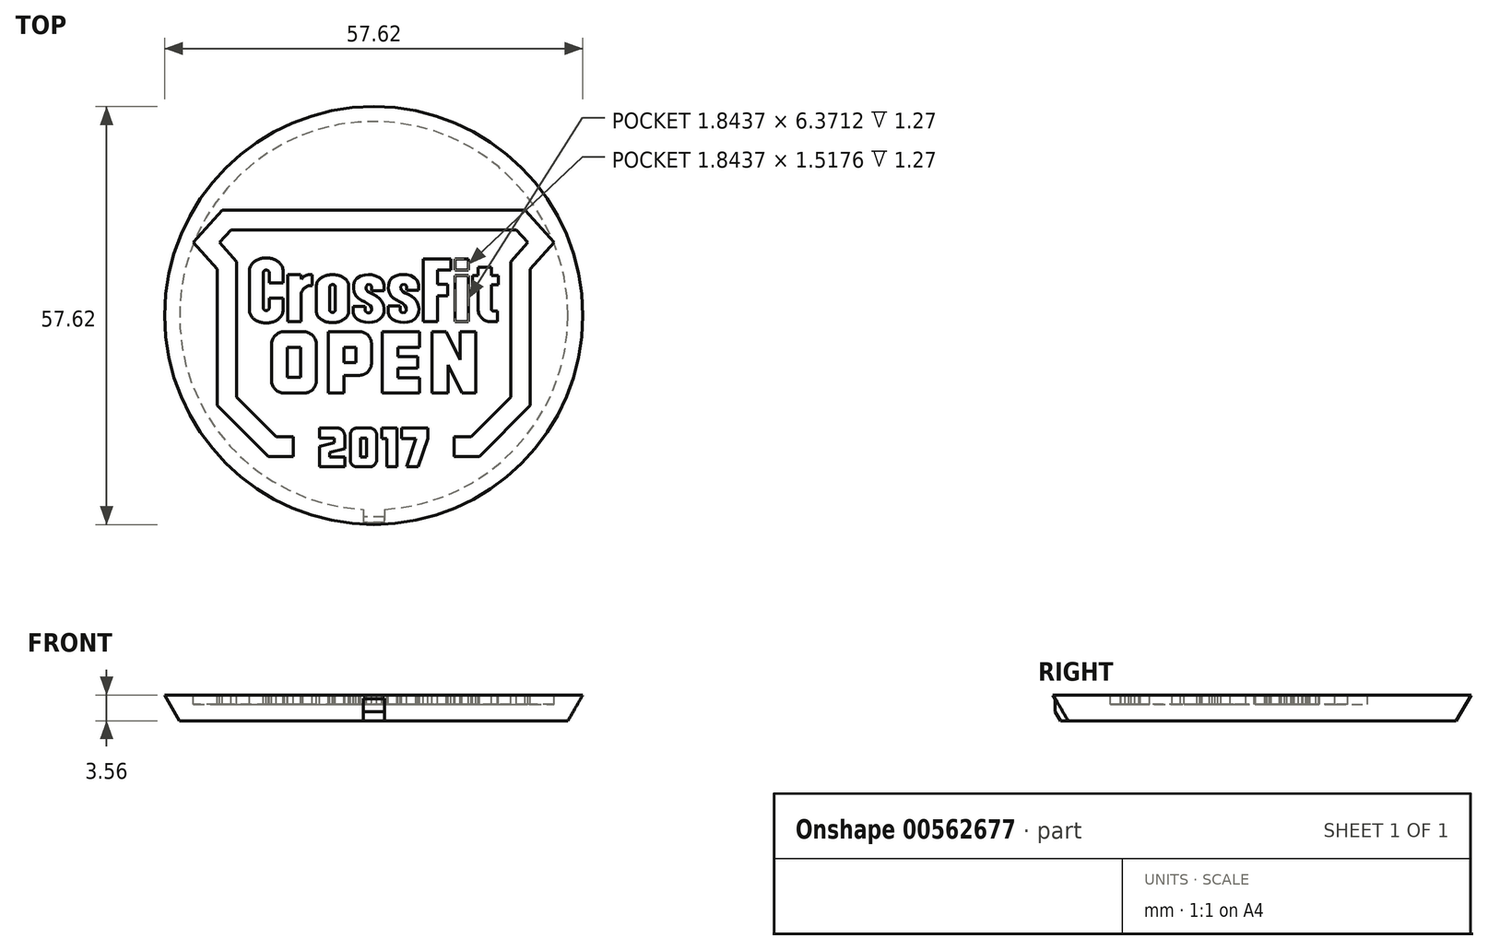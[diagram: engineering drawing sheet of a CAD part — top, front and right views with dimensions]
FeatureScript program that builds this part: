
annotation { "Feature Type Name" : "Feature", "Feature Type Description" : "" }
export const myFeature = defineFeature(function(context is Context, id is Id, definition is map)
    precondition{}
    {
        {
            var Q0;
            Q0=qCreatedBy(makeId("Top.planeOp"),FACE);
            var sketch = newSketch(context, id + "F0", { "sketchPlane" : qUnion([Q0])});
            skCircle(sketch, "E0", {"center": v(0, 0) * mm, "radius": 28.96 * mm});
            skSolve(sketch);
        }
        {
            var Q0;
            Q0=makeQuery(id+"F0.imprint","IMPRINT",FACE,{"disambiguationData":[TD([[makeQuery(id+"F0.imprint","IMPRINT",EDGE,{"derivedFrom":sQuery(id+"F0.wireOp",EDGE,"E0")}),1.0]])]});
            extrude(context, id + "F1", {"entities" : qUnion([Q0]), "depth" : 3.56 * mm, "offsetDistance" : 25.4 * mm});
        }
        {
            var Q0;
            Q0=makeQuery(id+"F1.opExtrude","CAP_FACE",FACE,{"disambiguationData":[OSD([sQuery(id+"F0.wireOp",EDGE,"E0")])],"isStart":false});
            var sketch = newSketch(context, id + "F2", { "sketchPlane" : qUnion([Q0])});
            skPoint(sketch, "E1", {"position": v(0.13, -0.67) * mm});
            skLineSegment(sketch, "E2", {"start": v(-15.2, 14.53) * mm, "end": v(-15.2, 11.82) * mm});
            skLineSegment(sketch, "E3", {"start": v(-15.2, 11.82) * mm, "end": v(-19.67, 11.82) * mm});
            skLineSegment(sketch, "E4", {"start": v(-19.67, 11.82) * mm, "end": v(-21.25, 10.06) * mm});
            skLineSegment(sketch, "E5", {"start": v(-21.25, 10.06) * mm, "end": v(-18.9, 7.43) * mm});
            skLineSegment(sketch, "E6", {"start": v(-18.9, 7.43) * mm, "end": v(-18.9, -11.25) * mm});
            skLineSegment(sketch, "E7", {"start": v(-18.9, -11.25) * mm, "end": v(-13.44, -16.74) * mm});
            skLineSegment(sketch, "E8", {"start": v(-13.44, -16.74) * mm, "end": v(-11.07, -16.74) * mm});
            skLineSegment(sketch, "E9", {"start": v(-11.07, -16.74) * mm, "end": v(-11.07, -19.45) * mm});
            skLineSegment(sketch, "E10", {"start": v(-11.07, -19.45) * mm, "end": v(-14.54, -19.45) * mm});
            skLineSegment(sketch, "E11", {"start": v(-14.54, -19.45) * mm, "end": v(-21.55, -12.4) * mm});
            skLineSegment(sketch, "E12", {"start": v(-21.55, -12.4) * mm, "end": v(-21.55, 6.37) * mm});
            skLineSegment(sketch, "E13", {"start": v(-21.55, 6.37) * mm, "end": v(-24.85, 10.06) * mm});
            skLineSegment(sketch, "E14", {"start": v(-24.85, 10.06) * mm, "end": v(-20.84, 14.53) * mm});
            skLineSegment(sketch, "E15", {"start": v(-20.84, 14.53) * mm, "end": v(-15.2, 14.53) * mm});
            skLineSegment(sketch, "E16", {"start": v(-14.42, 6) * mm, "end": v(-14.42, 4.47) * mm});
            skLineSegment(sketch, "E17", {"start": v(-14.42, 4.47) * mm, "end": v(-12.48, 4.47) * mm});
            skLineSegment(sketch, "E18", {"start": v(-12.48, 4.47) * mm, "end": v(-12.48, 6.3) * mm});
            skLineSegment(sketch, "E19", {"start": v(-17.15, 6.3) * mm, "end": v(-17.15, 0.62) * mm});
            skLineSegment(sketch, "E20", {"start": v(-14.42, 1) * mm, "end": v(-14.42, 2.43) * mm});
            skLineSegment(sketch, "E21", {"start": v(-14.42, 2.43) * mm, "end": v(-12.48, 2.43) * mm});
            skLineSegment(sketch, "E22", {"start": v(-12.48, 2.43) * mm, "end": v(-12.48, 0.62) * mm});
            skLineSegment(sketch, "E23", {"start": v(-15.2, 6) * mm, "end": v(-15.2, 1) * mm});
            skArc(sketch, "E24", {"start": v(-14.42, 6) * mm, "mid": v(-14.81, 6.27) * mm, "end": v(-15.2, 6) * mm});
            skArc(sketch, "E25", {"start": v(-15.2, 1) * mm, "mid": v(-14.81, 0.68) * mm, "end": v(-14.42, 1) * mm});
            skLineSegment(sketch, "E26", {"start": v(-9.97, 5) * mm, "end": v(-10.1, 5.63) * mm});
            skLineSegment(sketch, "E27", {"start": v(-10.1, 5.63) * mm, "end": v(-11.83, 5.63) * mm});
            skLineSegment(sketch, "E28", {"start": v(-11.83, 5.63) * mm, "end": v(-11.83, -0.85) * mm});
            skLineSegment(sketch, "E29", {"start": v(-11.83, -0.85) * mm, "end": v(-9.98, -0.85) * mm});
            skLineSegment(sketch, "E30", {"start": v(-9.98, -0.85) * mm, "end": v(-9.98, 3.1) * mm});
            skLineSegment(sketch, "E31", {"start": v(-8.5, 5.65) * mm, "end": v(-8.5, 4.11) * mm});
            skArc(sketch, "E32", {"start": v(-8.5, 5.65) * mm, "mid": v(-9.32, 5.53) * mm, "end": v(-9.97, 5) * mm});
            skArc(sketch, "E33", {"start": v(-8.5, 4.11) * mm, "mid": v(-9.44, 3.9) * mm, "end": v(-9.98, 3.1) * mm});
            skLineSegment(sketch, "E34", {"start": v(-7.89, 4.2) * mm, "end": v(-7.89, 0.46) * mm});
            skLineSegment(sketch, "E35", {"start": v(-3.47, 4.2) * mm, "end": v(-3.47, 0.46) * mm});
            skLineSegment(sketch, "E36", {"start": v(-6.05, 4.04) * mm, "end": v(-6.05, 0.68) * mm});
            skLineSegment(sketch, "E37", {"start": v(-5.3, 0.68) * mm, "end": v(-5.3, 4.04) * mm});
            skArc(sketch, "E38", {"start": v(-5.3, 4.04) * mm, "mid": v(-5.68, 4.28) * mm, "end": v(-6.05, 4.04) * mm});
            skArc(sketch, "E39", {"start": v(-6.05, 0.68) * mm, "mid": v(-5.68, 0.43) * mm, "end": v(-5.3, 0.68) * mm});
            skLineSegment(sketch, "E40", {"start": v(-5.68, 3.86) * mm, "end": v(-5.68, 0.84) * mm, "construction": true});
            skLineSegment(sketch, "E41", {"start": v(-7.89, 2.33) * mm, "end": v(-3.47, 2.33) * mm, "construction": true});
            skFitSpline(sketch, "E42.MirrorCS", {"points": [v(-3.47, 4.2) * mm, v(-3.93, 5.06) * mm, v(-4.62, 5.46) * mm, v(-5.68, 5.64) * mm], "startDerivative": vector(-0.46, 3.85) * mm, "endDerivative": vector(-4.22, 0.16) * mm});
            skFitSpline(sketch, "E43.MirrorCS", {"points": [v(-7.89, 0.46) * mm, v(-7.42, -0.4) * mm, v(-6.74, -0.8) * mm, v(-5.68, -0.98) * mm], "startDerivative": vector(0.46, -3.85) * mm, "endDerivative": vector(4.22, -0.16) * mm});
            skFitSpline(sketch, "E44.MirrorCS", {"points": [v(-3.47, 0.46) * mm, v(-3.93, -0.4) * mm, v(-4.62, -0.8) * mm, v(-5.68, -0.98) * mm], "startDerivative": vector(-0.46, -3.85) * mm, "endDerivative": vector(-4.22, -0.16) * mm});
            skFitSpline(sketch, "E45", {"points": [v(-17.15, 6.3) * mm, v(-16.64, 7.26) * mm, v(-16, 7.69) * mm, v(-14.81, 7.96) * mm], "startDerivative": vector(0.97, 4.15) * mm, "endDerivative": vector(4.22, 0.16) * mm});
            skLineSegment(sketch, "E46", {"start": v(-14.81, 5.84) * mm, "end": v(-14.81, 1.08) * mm, "construction": true});
            skFitSpline(sketch, "E47.MirrorCS", {"points": [v(-12.48, 6.3) * mm, v(-12.99, 7.26) * mm, v(-13.62, 7.69) * mm, v(-14.81, 7.96) * mm], "startDerivative": vector(-0.97, 4.15) * mm, "endDerivative": vector(-4.22, 0.16) * mm});
            skLineSegment(sketch, "E48", {"start": v(-17.15, 3.46) * mm, "end": v(-14.81, 3.46) * mm, "construction": true});
            skFitSpline(sketch, "E49.MirrorCS", {"points": [v(-17.15, 0.62) * mm, v(-16.64, -0.34) * mm, v(-16, -0.77) * mm, v(-14.81, -1.04) * mm], "startDerivative": vector(0.97, -4.15) * mm, "endDerivative": vector(4.22, -0.16) * mm});
            skFitSpline(sketch, "E50.MirrorCS", {"points": [v(-12.48, 0.62) * mm, v(-12.99, -0.34) * mm, v(-13.62, -0.77) * mm, v(-14.81, -1.04) * mm], "startDerivative": vector(-0.97, -4.15) * mm, "endDerivative": vector(-4.22, -0.16) * mm});
            skFitSpline(sketch, "E51.MirrorCS", {"points": [v(-7.89, 4.2) * mm, v(-7.42, 5.06) * mm, v(-6.74, 5.46) * mm, v(-5.68, 5.64) * mm], "startDerivative": vector(0.46, 3.85) * mm, "endDerivative": vector(4.22, 0.16) * mm});
            skLineSegment(sketch, "E52", {"start": v(-0.27, 4.07) * mm, "end": v(-0.27, 3.44) * mm});
            skLineSegment(sketch, "E53", {"start": v(-0.27, 3.44) * mm, "end": v(1.39, 3.44) * mm});
            skLineSegment(sketch, "E54", {"start": v(1.39, 3.44) * mm, "end": v(1.39, 4.25) * mm});
            skFitSpline(sketch, "E55", {"points": [v(1.39, 4.25) * mm, v(1.25, 4.73) * mm, v(0.96, 5.08) * mm, v(0.56, 5.36) * mm, v(0, 5.56) * mm, v(-0.4, 5.63) * mm, v(-0.7, 5.64) * mm, v(-1.07, 5.62) * mm, v(-1.62, 5.53) * mm, v(-2.03, 5.35) * mm, v(-2.4, 5.07) * mm, v(-2.62, 4.73) * mm, v(-2.76, 4.31) * mm, v(-2.8, 3.96) * mm, v(-2.78, 3.56) * mm, v(-2.7, 3.15) * mm, v(-2.47, 2.72) * mm, v(-2.25, 2.47) * mm, v(-1.97, 2.27) * mm, v(-1.61, 2.07) * mm, v(-1.3, 1.9) * mm, v(-1.02, 1.76) * mm, v(-0.75, 1.6) * mm, v(-0.5, 1.4) * mm, v(-0.41, 1.28) * mm, v(-0.32, 1.08) * mm, v(-0.3, 0.79) * mm, v(-0.34, 0.57) * mm, v(-0.46, 0.43) * mm, v(-0.64, 0.38) * mm, v(-0.84, 0.39) * mm, v(-1.03, 0.44) * mm, v(-1.16, 0.63) * mm], "startDerivative": vector(-2.14, 14.98) * mm, "endDerivative": vector(-3.94, 13.1) * mm});
            skLineSegment(sketch, "E56", {"start": v(-2.83, 0.39) * mm, "end": v(-2.83, 1.28) * mm});
            skLineSegment(sketch, "E57", {"start": v(-2.83, 1.28) * mm, "end": v(-1.16, 1.28) * mm});
            skLineSegment(sketch, "E58", {"start": v(-1.16, 1.28) * mm, "end": v(-1.16, 0.63) * mm});
            skFitSpline(sketch, "E59", {"points": [v(-2.83, 0.39) * mm, v(-2.67, -0.07) * mm, v(-2.35, -0.45) * mm, v(-1.98, -0.69) * mm, v(-1.5, -0.86) * mm, v(-1.03, -0.94) * mm, v(-0.7, -0.95) * mm, v(-0.34, -0.94) * mm, v(0.21, -0.84) * mm, v(0.6, -0.67) * mm, v(0.97, -0.39) * mm, v(1.22, -0.06) * mm, v(1.37, 0.3) * mm, v(1.42, 0.75) * mm, v(1.4, 1.11) * mm, v(1.3, 1.54) * mm, v(1.1, 1.95) * mm, v(0.87, 2.26) * mm, v(0.6, 2.5) * mm, v(0.3, 2.7) * mm, v(0, 2.88) * mm, v(-0.33, 3.05) * mm, v(-0.58, 3.18) * mm, v(-0.81, 3.31) * mm, v(-0.96, 3.44) * mm, v(-1.07, 3.64) * mm, v(-1.08, 3.86) * mm, v(-1.06, 4.07) * mm, v(-0.94, 4.24) * mm, v(-0.75, 4.3) * mm, v(-0.56, 4.29) * mm, v(-0.4, 4.23) * mm, v(-0.27, 4.07) * mm], "startDerivative": vector(2.14, -14.98) * mm, "endDerivative": vector(3.94, -13.1) * mm});
            skLineSegment(sketch, "E60", {"start": v(4.54, 4.08) * mm, "end": v(4.54, 3.45) * mm});
            skLineSegment(sketch, "E61", {"start": v(4.54, 3.45) * mm, "end": v(6.2, 3.45) * mm});
            skLineSegment(sketch, "E62", {"start": v(6.2, 3.45) * mm, "end": v(6.2, 4.26) * mm});
            skFitSpline(sketch, "E63", {"points": [v(6.2, 4.26) * mm, v(6.06, 4.74) * mm, v(5.77, 5.1) * mm, v(5.37, 5.37) * mm, v(4.81, 5.57) * mm, v(4.4, 5.64) * mm, v(4.11, 5.65) * mm, v(3.74, 5.63) * mm, v(3.2, 5.54) * mm, v(2.78, 5.36) * mm, v(2.42, 5.08) * mm, v(2.2, 4.74) * mm, v(2.05, 4.32) * mm, v(2.02, 3.97) * mm, v(2.03, 3.57) * mm, v(2.11, 3.16) * mm, v(2.34, 2.73) * mm, v(2.56, 2.48) * mm, v(2.84, 2.28) * mm, v(3.2, 2.08) * mm, v(3.52, 1.92) * mm, v(3.8, 1.77) * mm, v(4.06, 1.6) * mm, v(4.3, 1.41) * mm, v(4.4, 1.3) * mm, v(4.5, 1.09) * mm, v(4.5, 0.8) * mm, v(4.47, 0.58) * mm, v(4.35, 0.44) * mm, v(4.17, 0.39) * mm, v(3.97, 0.4) * mm, v(3.78, 0.45) * mm, v(3.65, 0.64) * mm], "startDerivative": vector(-2.14, 14.98) * mm, "endDerivative": vector(-3.94, 13.1) * mm});
            skLineSegment(sketch, "E64", {"start": v(1.98, 0.4) * mm, "end": v(1.98, 1.3) * mm});
            skLineSegment(sketch, "E65", {"start": v(1.98, 1.3) * mm, "end": v(3.65, 1.3) * mm});
            skLineSegment(sketch, "E66", {"start": v(3.65, 1.3) * mm, "end": v(3.65, 0.64) * mm});
            skFitSpline(sketch, "E67", {"points": [v(1.98, 0.4) * mm, v(2.14, -0.06) * mm, v(2.46, -0.44) * mm, v(2.83, -0.68) * mm, v(3.31, -0.85) * mm, v(3.78, -0.93) * mm, v(4.12, -0.95) * mm, v(4.47, -0.93) * mm, v(5.02, -0.83) * mm, v(5.42, -0.66) * mm, v(5.78, -0.38) * mm, v(6.03, -0.05) * mm, v(6.18, 0.32) * mm, v(6.23, 0.76) * mm, v(6.2, 1.12) * mm, v(6.12, 1.55) * mm, v(5.92, 1.96) * mm, v(5.68, 2.27) * mm, v(5.4, 2.5) * mm, v(5.1, 2.71) * mm, v(4.8, 2.89) * mm, v(4.48, 3.06) * mm, v(4.23, 3.2) * mm, v(4, 3.32) * mm, v(3.85, 3.45) * mm, v(3.74, 3.65) * mm, v(3.73, 3.87) * mm, v(3.75, 4.08) * mm, v(3.87, 4.25) * mm, v(4.06, 4.3) * mm, v(4.25, 4.3) * mm, v(4.42, 4.24) * mm, v(4.54, 4.08) * mm], "startDerivative": vector(2.14, -14.98) * mm, "endDerivative": vector(3.94, -13.1) * mm});
            skLineSegment(sketch, "E68", {"start": v(10.61, 7.8) * mm, "end": v(6.85, 7.8) * mm});
            skLineSegment(sketch, "E69", {"start": v(6.85, 7.8) * mm, "end": v(6.85, -0.85) * mm});
            skLineSegment(sketch, "E70", {"start": v(6.85, -0.85) * mm, "end": v(8.77, -0.85) * mm});
            skLineSegment(sketch, "E71", {"start": v(8.77, -0.85) * mm, "end": v(8.77, 2.7) * mm});
            skLineSegment(sketch, "E72", {"start": v(8.77, 2.7) * mm, "end": v(10.16, 2.7) * mm});
            skLineSegment(sketch, "E73", {"start": v(10.16, 2.7) * mm, "end": v(10.16, 4.29) * mm});
            skLineSegment(sketch, "E74", {"start": v(10.16, 4.29) * mm, "end": v(8.77, 4.29) * mm});
            skLineSegment(sketch, "E75", {"start": v(8.77, 4.29) * mm, "end": v(8.77, 6.28) * mm});
            skLineSegment(sketch, "E76", {"start": v(8.77, 6.28) * mm, "end": v(10.61, 6.28) * mm});
            skLineSegment(sketch, "E77", {"start": v(10.61, 6.28) * mm, "end": v(10.61, 7.8) * mm});
            skLineSegment(sketch, "E78", {"start": v(11.2, 7.8) * mm, "end": v(13.03, 7.8) * mm});
            skLineSegment(sketch, "E79", {"start": v(13.03, 7.8) * mm, "end": v(13.03, 6.28) * mm});
            skLineSegment(sketch, "E80", {"start": v(13.03, 6.28) * mm, "end": v(11.2, 6.28) * mm});
            skLineSegment(sketch, "E81", {"start": v(11.2, 6.28) * mm, "end": v(11.2, 7.8) * mm});
            skLineSegment(sketch, "E82", {"start": v(11.2, 5.52) * mm, "end": v(13.03, 5.52) * mm});
            skLineSegment(sketch, "E83", {"start": v(13.03, 5.52) * mm, "end": v(13.03, -0.85) * mm});
            skLineSegment(sketch, "E84", {"start": v(13.03, -0.85) * mm, "end": v(11.2, -0.85) * mm});
            skLineSegment(sketch, "E85", {"start": v(11.2, -0.85) * mm, "end": v(11.2, 5.52) * mm});
            skLineSegment(sketch, "E86", {"start": v(14.38, 6.63) * mm, "end": v(16.2, 6.63) * mm});
            skLineSegment(sketch, "E87", {"start": v(16.2, 6.63) * mm, "end": v(16.2, 5.52) * mm});
            skLineSegment(sketch, "E88", {"start": v(16.2, 5.52) * mm, "end": v(17.15, 5.52) * mm});
            skLineSegment(sketch, "E89", {"start": v(17.15, 5.52) * mm, "end": v(17.15, 4.23) * mm});
            skLineSegment(sketch, "E90", {"start": v(17.15, 4.23) * mm, "end": v(16.2, 4.23) * mm});
            skLineSegment(sketch, "E91", {"start": v(16.2, 4.23) * mm, "end": v(16.2, 0.92) * mm});
            skLineSegment(sketch, "E92", {"start": v(14.38, 6.63) * mm, "end": v(14.38, 5.52) * mm});
            skLineSegment(sketch, "E93", {"start": v(14.38, 5.52) * mm, "end": v(13.6, 5.52) * mm});
            skLineSegment(sketch, "E94", {"start": v(13.6, 5.52) * mm, "end": v(13.6, 4.23) * mm});
            skLineSegment(sketch, "E95", {"start": v(13.6, 4.23) * mm, "end": v(14.38, 4.23) * mm});
            skLineSegment(sketch, "E96", {"start": v(14.38, 4.23) * mm, "end": v(14.38, 0.85) * mm});
            skLineSegment(sketch, "E97", {"start": v(16.51, 0.61) * mm, "end": v(17.08, 0.61) * mm});
            skLineSegment(sketch, "E98", {"start": v(17.08, 0.61) * mm, "end": v(17.08, -0.85) * mm});
            skLineSegment(sketch, "E99", {"start": v(17.08, -0.85) * mm, "end": v(16.09, -0.85) * mm});
            skArc(sketch, "E100", {"start": v(14.38, 0.85) * mm, "mid": v(14.88, -0.35) * mm, "end": v(16.09, -0.85) * mm});
            skArc(sketch, "E101", {"start": v(16.2, 0.92) * mm, "mid": v(16.3, 0.7) * mm, "end": v(16.51, 0.61) * mm});
            skLineSegment(sketch, "E102", {"start": v(0, 18.62) * mm, "end": v(0, -25.74) * mm, "construction": true});
            skLineSegment(sketch, "E103.MirrorCS", {"start": v(15.2, 14.53) * mm, "end": v(15.2, 11.82) * mm});
            skLineSegment(sketch, "E104.MirrorCS", {"start": v(20.84, 14.53) * mm, "end": v(15.2, 14.53) * mm});
            skLineSegment(sketch, "E105.MirrorCS", {"start": v(24.85, 10.06) * mm, "end": v(20.84, 14.53) * mm});
            skLineSegment(sketch, "E106.MirrorCS", {"start": v(21.55, 6.37) * mm, "end": v(24.85, 10.06) * mm});
            skLineSegment(sketch, "E107.MirrorCS", {"start": v(21.55, -12.4) * mm, "end": v(21.55, 6.37) * mm});
            skLineSegment(sketch, "E108.MirrorCS", {"start": v(14.54, -19.45) * mm, "end": v(21.55, -12.4) * mm});
            skLineSegment(sketch, "E109.MirrorCS", {"start": v(11.07, -19.45) * mm, "end": v(14.54, -19.45) * mm});
            skLineSegment(sketch, "E110.MirrorCS", {"start": v(11.07, -16.74) * mm, "end": v(11.07, -19.45) * mm});
            skLineSegment(sketch, "E111.MirrorCS", {"start": v(13.44, -16.74) * mm, "end": v(11.07, -16.74) * mm});
            skLineSegment(sketch, "E112.MirrorCS", {"start": v(18.9, -11.25) * mm, "end": v(13.44, -16.74) * mm});
            skLineSegment(sketch, "E113.MirrorCS", {"start": v(18.9, 7.43) * mm, "end": v(18.9, -11.25) * mm});
            skLineSegment(sketch, "E114.MirrorCS", {"start": v(21.25, 10.06) * mm, "end": v(18.9, 7.43) * mm});
            skLineSegment(sketch, "E115.MirrorCS", {"start": v(19.67, 11.82) * mm, "end": v(21.25, 10.06) * mm});
            skLineSegment(sketch, "E116.MirrorCS", {"start": v(15.2, 11.82) * mm, "end": v(19.67, 11.82) * mm});
            skLineSegment(sketch, "E117", {"start": v(-5.1, -15.5) * mm, "end": v(-7.45, -15.5) * mm});
            skLineSegment(sketch, "E118", {"start": v(-7.45, -15.5) * mm, "end": v(-7.45, -16.87) * mm});
            skLineSegment(sketch, "E119", {"start": v(-7.45, -16.87) * mm, "end": v(-5.44, -16.87) * mm});
            skLineSegment(sketch, "E120", {"start": v(-5.44, -16.87) * mm, "end": v(-5.44, -17.52) * mm});
            skLineSegment(sketch, "E121", {"start": v(-5.44, -17.52) * mm, "end": v(-7.45, -18.02) * mm});
            skLineSegment(sketch, "E122", {"start": v(-7.45, -18.02) * mm, "end": v(-7.45, -20.86) * mm});
            skLineSegment(sketch, "E123", {"start": v(-7.45, -20.86) * mm, "end": v(-4, -20.86) * mm});
            skLineSegment(sketch, "E124", {"start": v(-4, -20.86) * mm, "end": v(-4, -19.5) * mm});
            skLineSegment(sketch, "E125", {"start": v(-4, -19.5) * mm, "end": v(-6.05, -19.5) * mm});
            skLineSegment(sketch, "E126", {"start": v(-6.05, -19.5) * mm, "end": v(-6.05, -18.84) * mm});
            skLineSegment(sketch, "E127", {"start": v(-6.05, -18.84) * mm, "end": v(-4, -18.34) * mm});
            skLineSegment(sketch, "E128", {"start": v(-4, -18.34) * mm, "end": v(-4, -16.6) * mm});
            skArc(sketch, "E129", {"start": v(-4, -16.6) * mm, "mid": v(-4.32, -15.83) * mm, "end": v(-5.1, -15.5) * mm});
            skLineSegment(sketch, "E130", {"start": v(-2.29, -15.5) * mm, "end": v(-0.56, -15.5) * mm});
            skLineSegment(sketch, "E131", {"start": v(-3.24, -16.46) * mm, "end": v(-3.24, -19.9) * mm});
            skLineSegment(sketch, "E132", {"start": v(-2.29, -20.86) * mm, "end": v(-0.56, -20.86) * mm});
            skLineSegment(sketch, "E133", {"start": v(0.4, -16.46) * mm, "end": v(0.4, -19.9) * mm});
            skArc(sketch, "E134", {"start": v(-2.29, -15.5) * mm, "mid": v(-2.96, -15.78) * mm, "end": v(-3.24, -16.46) * mm});
            skArc(sketch, "E135", {"start": v(0.4, -16.46) * mm, "mid": v(0.12, -15.78) * mm, "end": v(-0.56, -15.5) * mm});
            skArc(sketch, "E136", {"start": v(-3.24, -19.9) * mm, "mid": v(-2.96, -20.58) * mm, "end": v(-2.29, -20.86) * mm});
            skArc(sketch, "E137", {"start": v(-0.56, -20.86) * mm, "mid": v(0.12, -20.58) * mm, "end": v(0.4, -19.9) * mm});
            skLineSegment(sketch, "E138", {"start": v(1.1, -15.5) * mm, "end": v(3.22, -15.5) * mm});
            skLineSegment(sketch, "E139", {"start": v(3.22, -15.5) * mm, "end": v(3.22, -20.86) * mm});
            skLineSegment(sketch, "E140", {"start": v(3.22, -20.86) * mm, "end": v(1.77, -20.86) * mm});
            skLineSegment(sketch, "E141", {"start": v(1.77, -20.86) * mm, "end": v(1.77, -16.97) * mm});
            skLineSegment(sketch, "E142", {"start": v(1.77, -16.97) * mm, "end": v(1.1, -16.97) * mm});
            skLineSegment(sketch, "E143", {"start": v(1.1, -16.97) * mm, "end": v(1.1, -15.5) * mm});
            skLineSegment(sketch, "E144", {"start": v(3.84, -15.5) * mm, "end": v(7.43, -15.5) * mm});
            skLineSegment(sketch, "E145", {"start": v(7.43, -15.5) * mm, "end": v(7.43, -16.97) * mm});
            skLineSegment(sketch, "E146", {"start": v(7.43, -16.97) * mm, "end": v(6.14, -20.86) * mm});
            skLineSegment(sketch, "E147", {"start": v(6.14, -20.86) * mm, "end": v(4.53, -20.86) * mm});
            skLineSegment(sketch, "E148", {"start": v(4.53, -20.86) * mm, "end": v(5.83, -16.97) * mm});
            skLineSegment(sketch, "E149", {"start": v(5.83, -16.97) * mm, "end": v(3.84, -16.97) * mm});
            skLineSegment(sketch, "E150", {"start": v(3.84, -16.97) * mm, "end": v(3.84, -15.5) * mm});
            skLineSegment(sketch, "E151", {"start": v(-1.85, -16.87) * mm, "end": v(-0.99, -16.87) * mm});
            skLineSegment(sketch, "E152", {"start": v(-0.99, -16.87) * mm, "end": v(-0.99, -19.51) * mm});
            skLineSegment(sketch, "E153", {"start": v(-0.99, -19.51) * mm, "end": v(-1.85, -19.51) * mm});
            skLineSegment(sketch, "E154", {"start": v(-1.85, -19.51) * mm, "end": v(-1.85, -16.87) * mm});
            skLineSegment(sketch, "E155", {"start": v(-15.2, 14.53) * mm, "end": v(15.2, 14.53) * mm});
            skLineSegment(sketch, "E156", {"start": v(-15.2, 11.82) * mm, "end": v(15.2, 11.82) * mm});
            skLineSegment(sketch, "E157", {"start": v(-14.1, -4.04) * mm, "end": v(-14.1, -8.95) * mm});
            skLineSegment(sketch, "E158", {"start": v(-12.3, -10.7) * mm, "end": v(-9.74, -10.7) * mm});
            skLineSegment(sketch, "E159", {"start": v(-7.9, -8.95) * mm, "end": v(-7.9, -4.04) * mm});
            skLineSegment(sketch, "E160", {"start": v(-12.3, -2.22) * mm, "end": v(-9.74, -2.22) * mm});
            skArc(sketch, "E161", {"start": v(-12.3, -2.22) * mm, "mid": v(-13.57, -2.77) * mm, "end": v(-14.1, -4.04) * mm});
            skArc(sketch, "E162", {"start": v(-7.9, -4.04) * mm, "mid": v(-8.44, -2.75) * mm, "end": v(-9.74, -2.22) * mm});
            skArc(sketch, "E163", {"start": v(-9.74, -10.7) * mm, "mid": v(-8.44, -10.22) * mm, "end": v(-7.9, -8.95) * mm});
            skArc(sketch, "E164", {"start": v(-14.1, -8.95) * mm, "mid": v(-13.55, -10.19) * mm, "end": v(-12.3, -10.7) * mm});
            skLineSegment(sketch, "E165.bottom", {"start": v(-11.9, -4.38) * mm, "end": v(-10.07, -4.38) * mm});
            skLineSegment(sketch, "E165.top", {"start": v(-11.9, -8.53) * mm, "end": v(-10.07, -8.53) * mm});
            skLineSegment(sketch, "E165.left", {"start": v(-11.9, -4.38) * mm, "end": v(-11.9, -8.53) * mm});
            skLineSegment(sketch, "E165.right", {"start": v(-10.07, -4.38) * mm, "end": v(-10.07, -8.53) * mm});
            skLineSegment(sketch, "E166", {"start": v(-6.28, -2.22) * mm, "end": v(-6.28, -10.7) * mm});
            skLineSegment(sketch, "E167", {"start": v(-6.28, -10.7) * mm, "end": v(-4.11, -10.7) * mm});
            skLineSegment(sketch, "E168", {"start": v(-4.11, -10.7) * mm, "end": v(-4.11, -8.24) * mm});
            skLineSegment(sketch, "E169", {"start": v(-4.11, -8.24) * mm, "end": v(-2.07, -8.24) * mm});
            skLineSegment(sketch, "E170", {"start": v(-6.28, -2.22) * mm, "end": v(-2.07, -2.22) * mm});
            skLineSegment(sketch, "E171", {"start": v(-0.3, -3.92) * mm, "end": v(-0.3, -6.53) * mm});
            skArc(sketch, "E172", {"start": v(-0.3, -3.92) * mm, "mid": v(-0.83, -2.7) * mm, "end": v(-2.07, -2.22) * mm});
            skArc(sketch, "E173", {"start": v(-2.07, -8.24) * mm, "mid": v(-0.83, -7.76) * mm, "end": v(-0.3, -6.53) * mm});
            skLineSegment(sketch, "E174.bottom", {"start": v(-4.13, -4.4) * mm, "end": v(-2.47, -4.4) * mm});
            skLineSegment(sketch, "E174.top", {"start": v(-4.13, -6.49) * mm, "end": v(-2.47, -6.49) * mm});
            skLineSegment(sketch, "E174.left", {"start": v(-4.13, -4.4) * mm, "end": v(-4.13, -6.49) * mm});
            skLineSegment(sketch, "E174.right", {"start": v(-2.47, -4.4) * mm, "end": v(-2.47, -6.49) * mm});
            skLineSegment(sketch, "E175", {"start": v(1.15, -2.22) * mm, "end": v(1.15, -10.7) * mm});
            skLineSegment(sketch, "E176", {"start": v(1.15, -10.7) * mm, "end": v(6.3, -10.7) * mm});
            skLineSegment(sketch, "E177", {"start": v(6.3, -10.7) * mm, "end": v(6.3, -8.56) * mm});
            skLineSegment(sketch, "E178", {"start": v(6.3, -8.56) * mm, "end": v(3.35, -8.56) * mm});
            skLineSegment(sketch, "E179", {"start": v(3.35, -8.56) * mm, "end": v(3.35, -7.26) * mm});
            skLineSegment(sketch, "E180", {"start": v(3.35, -7.26) * mm, "end": v(6.04, -7.26) * mm});
            skLineSegment(sketch, "E181", {"start": v(6.04, -7.26) * mm, "end": v(6.04, -5.67) * mm});
            skLineSegment(sketch, "E182", {"start": v(6.04, -5.67) * mm, "end": v(3.35, -5.66) * mm});
            skLineSegment(sketch, "E183", {"start": v(3.35, -5.66) * mm, "end": v(3.35, -4.36) * mm});
            skLineSegment(sketch, "E184", {"start": v(3.35, -4.36) * mm, "end": v(6.3, -4.36) * mm});
            skLineSegment(sketch, "E185", {"start": v(6.3, -4.36) * mm, "end": v(6.3, -2.22) * mm});
            skLineSegment(sketch, "E186", {"start": v(6.3, -2.22) * mm, "end": v(1.15, -2.22) * mm});
            skLineSegment(sketch, "E187", {"start": v(8.05, -2.22) * mm, "end": v(8.05, -10.7) * mm});
            skLineSegment(sketch, "E188", {"start": v(8.05, -10.7) * mm, "end": v(10.24, -10.7) * mm});
            skLineSegment(sketch, "E189", {"start": v(10.24, -10.7) * mm, "end": v(10.24, -6.84) * mm});
            skLineSegment(sketch, "E190", {"start": v(10.24, -6.84) * mm, "end": v(12.13, -10.7) * mm});
            skLineSegment(sketch, "E191", {"start": v(12.13, -10.7) * mm, "end": v(14.07, -10.7) * mm});
            skLineSegment(sketch, "E192", {"start": v(14.07, -10.7) * mm, "end": v(14.07, -2.22) * mm});
            skLineSegment(sketch, "E193", {"start": v(14.07, -2.22) * mm, "end": v(11.89, -2.22) * mm});
            skLineSegment(sketch, "E194", {"start": v(11.89, -2.22) * mm, "end": v(11.89, -6.08) * mm});
            skLineSegment(sketch, "E195", {"start": v(11.89, -6.08) * mm, "end": v(10, -2.22) * mm});
            skLineSegment(sketch, "E196", {"start": v(10, -2.22) * mm, "end": v(8.05, -2.22) * mm});
            skCircle(sketch, "E197", {"center": v(0, 0) * mm, "radius": 28.9 * mm});
            skSolve(sketch);
        }
        {
            var Q0;
            Q0=makeQuery(id+"F2.imprint","IMPRINT",FACE,{"disambiguationData":[TD([[makeQuery(id+"F2.imprint","IMPRINT",EDGE,{"derivedFrom":sQuery(id+"F2.wireOp",EDGE,"E2")}),1.0]])]});
            var Q1;
            Q1=makeQuery(id+"F2.imprint","IMPRINT",FACE,{"disambiguationData":[TD([[makeQuery(id+"F2.imprint","IMPRINT",EDGE,{"derivedFrom":sQuery(id+"F2.wireOp",EDGE,"E103.MirrorCS")}),1.0]])]});
            var Q2;
            Q2=makeQuery(id+"F2.imprint","IMPRINT",FACE,{"disambiguationData":[TD([[makeQuery(id+"F2.imprint","IMPRINT",EDGE,{"derivedFrom":sQuery(id+"F2.wireOp",EDGE,"E2")}),-1.0]])]});
            var Q3;
            Q3=makeQuery(id+"F2.imprint","IMPRINT",FACE,{"disambiguationData":[TD([[makeQuery(id+"F2.imprint","IMPRINT",EDGE,{"derivedFrom":sQuery(id+"F2.wireOp",EDGE,"E16")}),1.0]])]});
            var Q4;
            Q4=makeQuery(id+"F2.imprint","IMPRINT",FACE,{"disambiguationData":[TD([[makeQuery(id+"F2.imprint","IMPRINT",EDGE,{"derivedFrom":sQuery(id+"F2.wireOp",EDGE,"E26")}),1.0]])]});
            var Q5;
            Q5=makeQuery(id+"F2.imprint","IMPRINT",FACE,{"disambiguationData":[TD([[makeQuery(id+"F2.imprint","IMPRINT",EDGE,{"derivedFrom":sQuery(id+"F2.wireOp",EDGE,"E34")}),1.0]])]});
            var Q6;
            Q6=makeQuery(id+"F2.imprint","IMPRINT",FACE,{"disambiguationData":[TD([[makeQuery(id+"F2.imprint","IMPRINT",EDGE,{"derivedFrom":sQuery(id+"F2.wireOp",EDGE,"E52")}),1.0]])]});
            var Q7;
            Q7=makeQuery(id+"F2.imprint","IMPRINT",FACE,{"disambiguationData":[TD([[makeQuery(id+"F2.imprint","IMPRINT",EDGE,{"derivedFrom":sQuery(id+"F2.wireOp",EDGE,"E60")}),1.0]])]});
            var Q8;
            Q8=makeQuery(id+"F2.imprint","IMPRINT",FACE,{"disambiguationData":[TD([[makeQuery(id+"F2.imprint","IMPRINT",EDGE,{"derivedFrom":sQuery(id+"F2.wireOp",EDGE,"E68")}),1.0]])]});
            var Q9;
            Q9=makeQuery(id+"F2.imprint","IMPRINT",FACE,{"disambiguationData":[TD([[makeQuery(id+"F2.imprint","IMPRINT",EDGE,{"derivedFrom":sQuery(id+"F2.wireOp",EDGE,"E82")}),-1.0]])]});
            var Q10;
            Q10=makeQuery(id+"F2.imprint","IMPRINT",FACE,{"disambiguationData":[TD([[makeQuery(id+"F2.imprint","IMPRINT",EDGE,{"derivedFrom":sQuery(id+"F2.wireOp",EDGE,"E78")}),-1.0]])]});
            var Q11;
            Q11=makeQuery(id+"F2.imprint","IMPRINT",FACE,{"disambiguationData":[TD([[makeQuery(id+"F2.imprint","IMPRINT",EDGE,{"derivedFrom":sQuery(id+"F2.wireOp",EDGE,"E86")}),-1.0]])]});
            var Q12;
            Q12=makeQuery(id+"F2.imprint","IMPRINT",FACE,{"disambiguationData":[TD([[makeQuery(id+"F2.imprint","IMPRINT",EDGE,{"derivedFrom":sQuery(id+"F2.wireOp",EDGE,"E187")}),1.0]])]});
            var Q13;
            Q13=makeQuery(id+"F2.imprint","IMPRINT",FACE,{"disambiguationData":[TD([[makeQuery(id+"F2.imprint","IMPRINT",EDGE,{"derivedFrom":sQuery(id+"F2.wireOp",EDGE,"E175")}),1.0]])]});
            var Q14;
            Q14=makeQuery(id+"F2.imprint","IMPRINT",FACE,{"disambiguationData":[TD([[makeQuery(id+"F2.imprint","IMPRINT",EDGE,{"derivedFrom":sQuery(id+"F2.wireOp",EDGE,"E166")}),1.0]])]});
            var Q15;
            Q15=makeQuery(id+"F2.imprint","IMPRINT",FACE,{"disambiguationData":[TD([[makeQuery(id+"F2.imprint","IMPRINT",EDGE,{"derivedFrom":sQuery(id+"F2.wireOp",EDGE,"E157")}),1.0]])]});
            var Q16;
            Q16=makeQuery(id+"F2.imprint","IMPRINT",FACE,{"disambiguationData":[TD([[makeQuery(id+"F2.imprint","IMPRINT",EDGE,{"derivedFrom":sQuery(id+"F2.wireOp",EDGE,"E117")}),1.0]])]});
            var Q17;
            Q17=makeQuery(id+"F2.imprint","IMPRINT",FACE,{"disambiguationData":[TD([[makeQuery(id+"F2.imprint","IMPRINT",EDGE,{"derivedFrom":sQuery(id+"F2.wireOp",EDGE,"E130")}),-1.0]])]});
            var Q18;
            Q18=makeQuery(id+"F2.imprint","IMPRINT",FACE,{"disambiguationData":[TD([[makeQuery(id+"F2.imprint","IMPRINT",EDGE,{"derivedFrom":sQuery(id+"F2.wireOp",EDGE,"E138")}),-1.0]])]});
            var Q19;
            Q19=makeQuery(id+"F2.imprint","IMPRINT",FACE,{"disambiguationData":[TD([[makeQuery(id+"F2.imprint","IMPRINT",EDGE,{"derivedFrom":sQuery(id+"F2.wireOp",EDGE,"E144")}),-1.0]])]});
            extrude(context, id + "F3", {"entities" : qUnion([Q0, Q1, Q2, Q3, Q4, Q5, Q6, Q7, Q8, Q9, Q10, Q11, Q12, Q13, Q14, Q15, Q16, Q17, Q18, Q19]), "operationType" : NewBodyOperationType.REMOVE, "oppositeDirection" : true, "depth" : 1.27 * mm, "offsetDistance" : 25.4 * mm});
        }
        {
            var Q0;
            Q0=makeQuery(id+"F1.opExtrude","CAP_EDGE",EDGE,{"disambiguationData":[OSD([sQuery(id+"F0.wireOp",EDGE,"E0")])],"isStart":true});
            chamfer(context, id + "F4", {"entities" : qUnion([Q0]), "chamferType" : ChamferType.OFFSET_ANGLE, "width" : 3.8 * mm, "oppositeDirection" : false, "angle" : 30 * degree, "tangentPropagation" : true});
        }
        {
            var Q0;
            {var subQ0=sQuery(id+"F0.wireOp",EDGE,"E0");Q0=makeQuery(id+"F3.boolean.opBoolean","SPLIT",FACE,{"disambiguationData":[TD([makeQuery(id+"F1.opExtrude","SWEPT_FACE",FACE,{"disambiguationData":[OSD([subQ0])]})])],"derivedFrom":makeQuery(id+"F1.opExtrude","CAP_FACE",FACE,{"disambiguationData":[OSD([subQ0])],"isStart":false})});}
            var sketch = newSketch(context, id + "F5", { "sketchPlane" : qUnion([Q0])});
            skCircle(sketch, "E198.0", {"center": v(0, 0) * mm, "radius": 26.76 * mm});
            skLineSegment(sketch, "E199.bottom", {"start": v(-1.46, -28.5) * mm, "end": v(1.46, -28.5) * mm});
            skLineSegment(sketch, "E199.top", {"start": v(-1.46, -26.72) * mm, "end": v(1.46, -26.72) * mm});
            skLineSegment(sketch, "E199.left", {"start": v(-1.46, -28.5) * mm, "end": v(-1.46, -26.72) * mm});
            skLineSegment(sketch, "E199.right", {"start": v(1.46, -28.5) * mm, "end": v(1.46, -26.72) * mm});
            skSolve(sketch);
        }
        {
            var Q0;
            Q0=makeQuery(id+"F5.imprint","IMPRINT",FACE,{"disambiguationData":[TD([[makeQuery(id+"F5.imprint","IMPRINT",EDGE,{"derivedFrom":sQuery(id+"F5.wireOp",EDGE,"E199.bottom")}),1.0]])]});
            var Q1;
            Q1=makeQuery(id+"F1.opExtrude","CAP_FACE",FACE,{"disambiguationData":[OSD([sQuery(id+"F0.wireOp",EDGE,"E0")])],"isStart":true});
            extrude(context, id + "F6", {"entities" : qUnion([Q0]), "operationType" : NewBodyOperationType.ADD, "endBound" : BoundingType.UP_TO_SURFACE, "oppositeDirection" : true, "depth" : 25.4 * mm, "endBoundEntityFace" : qUnion([Q1]), "offsetDistance" : 0.25 * mm});
        }
        {
            var Q0;
            Q0=makeQuery(id+"F6.opExtrude","CAP_EDGE",EDGE,{"disambiguationData":[OSD([sQuery(id+"F5.wireOp",EDGE,"E199.bottom")])],"isStart":false});
            chamfer(context, id + "F7", {"entities" : qUnion([Q0]), "chamferType" : ChamferType.OFFSET_ANGLE, "width" : 1.27 * mm, "oppositeDirection" : true, "angle" : 30 * degree, "tangentPropagation" : true});
        }
    });
